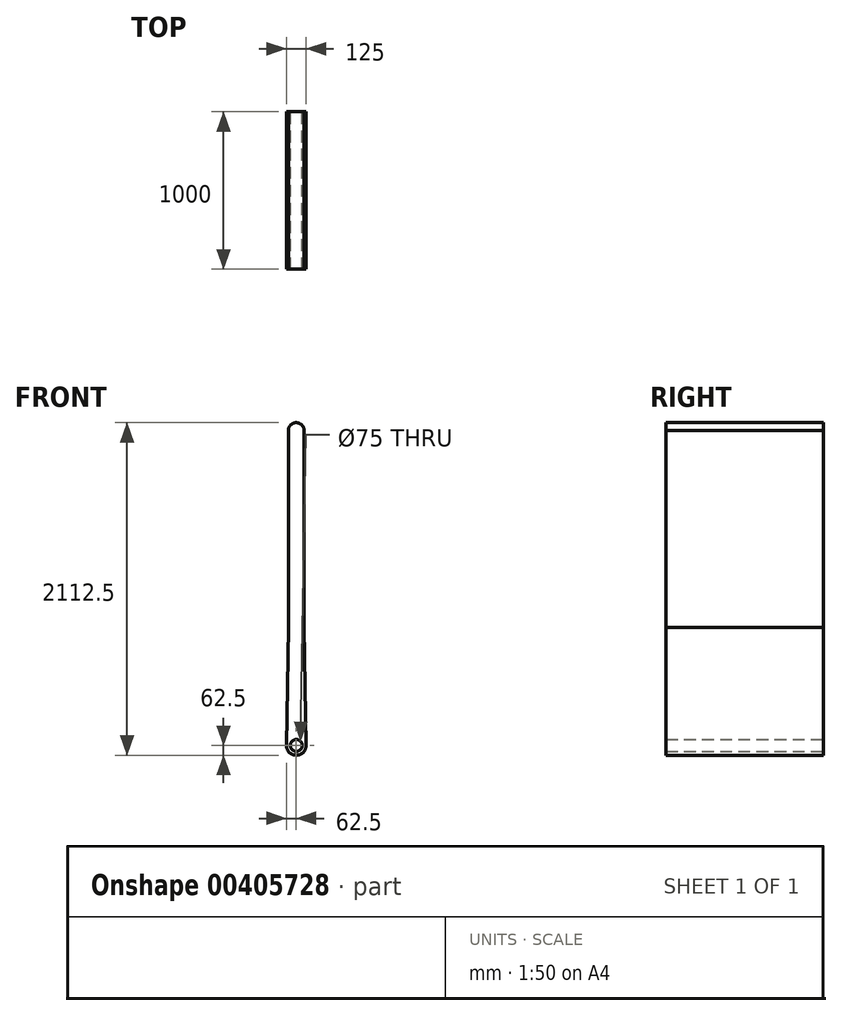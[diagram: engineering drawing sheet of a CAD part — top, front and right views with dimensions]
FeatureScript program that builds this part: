
annotation { "Feature Type Name" : "Feature", "Feature Type Description" : "" }
export const myFeature = defineFeature(function(context is Context, id is Id, definition is map)
    precondition{}
    {
        {
            var Q0;
            Q0=qCreatedBy(makeId("Front.planeOp"),FACE);
            var sketch = newSketch(context, id + "F0", { "sketchPlane" : qUnion([Q0])});
            skCircle(sketch, "E0", {"center": v(0, 0) * mm, "radius": 37.5 * mm});
            skCircle(sketch, "E1", {"center": v(0, 0) * mm, "radius": 62.5 * mm});
            skCircle(sketch, "E2", {"center": v(0, 750) * mm, "radius": 50 * mm});
            skLineSegment(sketch, "E3", {"start": v(50, 750.83) * mm, "end": v(62.5, 0) * mm});
            skLineSegment(sketch, "E4", {"start": v(-50, 750.83) * mm, "end": v(-62.5, 1.04) * mm});
            skCircle(sketch, "E5", {"center": v(0, 2000) * mm, "radius": 50 * mm});
            skLineSegment(sketch, "E6", {"start": v(-50, 750.83) * mm, "end": v(-50, 2000.83) * mm});
            skLineSegment(sketch, "E7", {"start": v(50, 750.83) * mm, "end": v(50, 2000.83) * mm});
            skArc(sketch, "E8", {"start": v(37.5, 0) * mm, "mid": v(26.52, 26.52) * mm, "end": v(0, 37.5) * mm});
            skLineSegment(sketch, "E9", {"start": v(0, 37.5) * mm, "end": v(0, 0) * mm});
            skSolve(sketch);
        }
        {
            var Q0;
            Q0 = qSketchRegion(id + "F0", true);
            extrude(context, id + "F1", {"entities" : qUnion([Q0]), "depth" : 1000 * mm});
        }
    });
